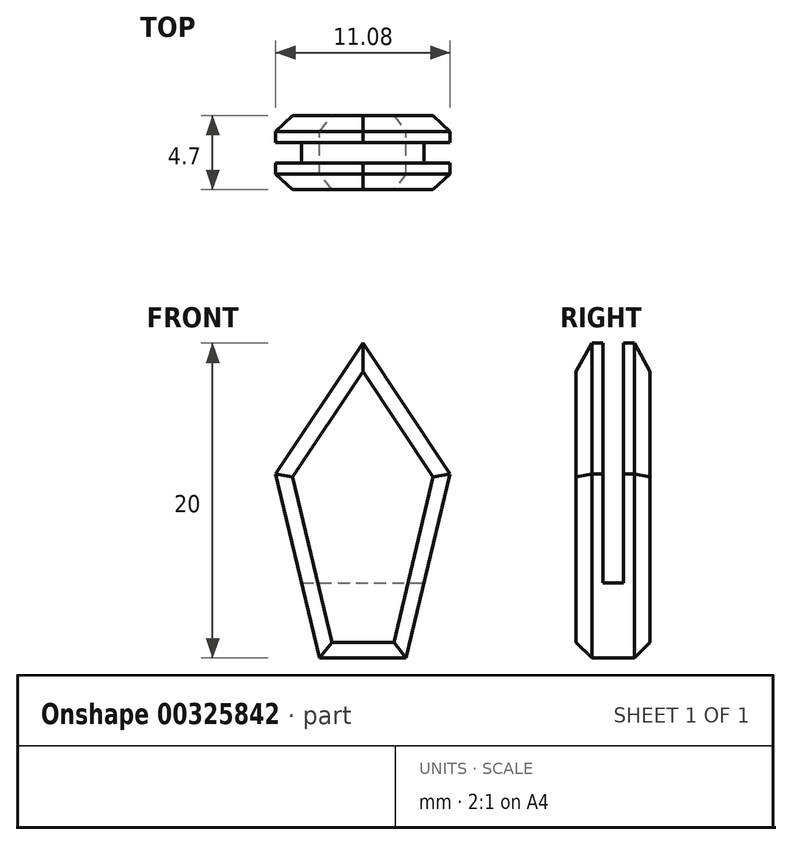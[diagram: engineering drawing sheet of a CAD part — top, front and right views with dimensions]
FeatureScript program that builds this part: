
annotation { "Feature Type Name" : "Feature", "Feature Type Description" : "" }
export const myFeature = defineFeature(function(context is Context, id is Id, definition is map)
    precondition{}
    {
        {
            var Q0;
            Q0=qCreatedBy(makeId("Front.planeOp"),FACE);
            var sketch = newSketch(context, id + "F0", { "sketchPlane" : qUnion([Q0])});
            skLineSegment(sketch, "E0", {"start": v(-2.75, 0) * mm, "end": v(2.75, 0) * mm});
            skLineSegment(sketch, "E1", {"start": v(-2.75, 0) * mm, "end": v(-5.54, 11.67) * mm});
            skLineSegment(sketch, "E2", {"start": v(2.75, 0) * mm, "end": v(5.54, 11.67) * mm});
            skLineSegment(sketch, "E3", {"start": v(5.54, 11.67) * mm, "end": v(0, 20) * mm});
            skLineSegment(sketch, "E4", {"start": v(0, 20) * mm, "end": v(-5.54, 11.67) * mm});
            skSolve(sketch);
        }
        {
            var Q0;
            Q0=qSketchRegion(id+"F0",true);
            var Q1;
            Q1=makeQuery(id+"F0.imprint","IMPRINT",FACE,{"disambiguationData":[TD([[makeQuery(id+"F0.imprint","IMPRINT",EDGE,{"derivedFrom":sQuery(id+"F0.wireOp",EDGE,"E0")}),1.0]])]});
            extrude(context, id + "F1", {"entities" : qUnion([Q0, Q1]), "depth" : 4.7 * mm});
        }
        {
            var Q0;
            Q0=qCreatedBy(makeId("Right.planeOp"),FACE);
            var sketch = newSketch(context, id + "F2", { "sketchPlane" : qUnion([Q0])});
            skLineSegment(sketch, "E5.bottom", {"start": v(-3, 24.75) * mm, "end": v(-1.7, 24.75) * mm});
            skLineSegment(sketch, "E5.top", {"start": v(-3, 4.75) * mm, "end": v(-1.7, 4.75) * mm});
            skLineSegment(sketch, "E5.left", {"start": v(-3, 24.75) * mm, "end": v(-3, 4.75) * mm});
            skLineSegment(sketch, "E5.right", {"start": v(-1.7, 24.75) * mm, "end": v(-1.7, 4.75) * mm});
            skCircle(sketch, "E6", {"center": v(-2.35, 4.75) * mm, "radius": 2.35 * mm, "construction": true});
            skSolve(sketch);
        }
        {
            var Q0;
            Q0=makeQuery(id+"F2.imprint","IMPRINT",FACE,{"disambiguationData":[TD([[makeQuery(id+"F2.imprint","IMPRINT",EDGE,{"derivedFrom":sQuery(id+"F2.wireOp",EDGE,"E5.bottom")}),-1.0]])]});
            extrude(context, id + "F3", {"entities" : qUnion([Q0]), "operationType" : NewBodyOperationType.REMOVE, "endBound" : BoundingType.SYMMETRIC, "oppositeDirection" : true, "depth" : 20 * mm});
        }
        {
            var Q0;
            Q0=makeQuery(id+"F1.opExtrude","CAP_FACE",FACE,{"disambiguationData":[OSD([sQuery(id+"F0.wireOp",EDGE,"E0"),sQuery(id+"F0.wireOp",EDGE,"E1"),sQuery(id+"F0.wireOp",EDGE,"E2"),sQuery(id+"F0.wireOp",EDGE,"E3"),sQuery(id+"F0.wireOp",EDGE,"E4")])],"isStart":false});
            var Q1;
            Q1=makeQuery(id+"F1.opExtrude","CAP_FACE",FACE,{"disambiguationData":[OSD([sQuery(id+"F0.wireOp",EDGE,"E0"),sQuery(id+"F0.wireOp",EDGE,"E1"),sQuery(id+"F0.wireOp",EDGE,"E2"),sQuery(id+"F0.wireOp",EDGE,"E3"),sQuery(id+"F0.wireOp",EDGE,"E4")])],"isStart":true});
            chamfer(context, id + "F4", {"entities" : qUnion([Q0, Q1]), "width" : 1 * mm, "tangentPropagation" : true});
        }
    });
